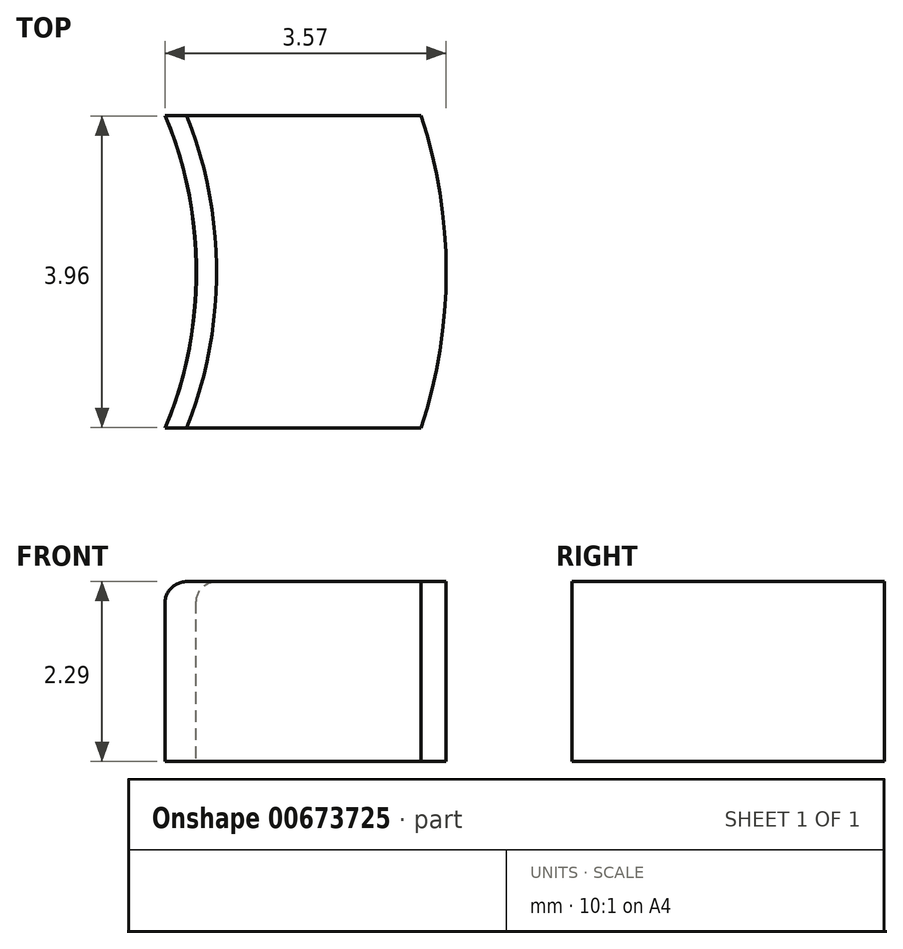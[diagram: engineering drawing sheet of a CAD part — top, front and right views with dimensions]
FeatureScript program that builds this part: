
annotation { "Feature Type Name" : "Feature", "Feature Type Description" : "" }
export const myFeature = defineFeature(function(context is Context, id is Id, definition is map)
    precondition{}
    {
        {
            var Q0;
            Q0=qCreatedBy(makeId("Top.planeOp"),FACE);
            var sketch = newSketch(context, id + "F0", { "sketchPlane" : qUnion([Q0])});
            skCircle(sketch, "E0", {"center": v(0, 0) * mm, "radius": 6.35 * mm});
            skEllipse(sketch, "E1", {"center": v(0, 0) * mm, "majorRadius": 4.11 * mm, "minorRadius": 3.18 * mm, "majorAxis": v(0, 1)});
            skSolve(sketch);
        }
        {
            var Q0;
            Q0=makeQuery(id+"F0.imprint","IMPRINT",FACE,{"disambiguationData":[TD([[makeQuery(id+"F0.imprint","IMPRINT",EDGE,{"derivedFrom":sQuery(id+"F0.wireOp",EDGE,"E0")}),1.0]])]});
            extrude(context, id + "F1", {"entities" : qUnion([Q0]), "depth" : 2.3 * mm, "offsetDistance" : 25.4 * mm});
        }
        {
            var Q0;
            Q0=makeQuery(id+"F1.opExtrude","CAP_EDGE",EDGE,{"disambiguationData":[OSD([sQuery(id+"F0.wireOp",EDGE,"E1")])],"isStart":false});
            fillet(context, id + "F2", {"entities" : qUnion([Q0]), "radius" : 0.25 * mm, "tangentPropagation" : true, "allowEdgeOverflow" : false});
        }
        {
            var Q0;
            Q0=makeQuery(id+"F1.opExtrude","CAP_FACE",FACE,{"disambiguationData":[OSD([sQuery(id+"F0.wireOp",EDGE,"E0"),sQuery(id+"F0.wireOp",EDGE,"E1")])],"isStart":false});
            var sketch = newSketch(context, id + "F3", { "sketchPlane" : qUnion([Q0])});
            skLineSegment(sketch, "E2.bottom", {"start": v(7, -1.98) * mm, "end": v(-1.33, -1.98) * mm});
            skLineSegment(sketch, "E2.top", {"start": v(7, 1.98) * mm, "end": v(-1.33, 1.98) * mm});
            skLineSegment(sketch, "E2.left", {"start": v(7, -1.98) * mm, "end": v(7, 1.98) * mm});
            skLineSegment(sketch, "E2.right", {"start": v(-1.33, -1.98) * mm, "end": v(-1.33, 1.98) * mm});
            skPoint(sketch, "E2.middle", {"position": v(2.84, 0) * mm});
            skSolve(sketch);
        }
        {
            var Q0;
            Q0 = qSketchRegion(id + "F3", true);
            extrude(context, id + "F4", {"entities" : qUnion([Q0]), "operationType" : NewBodyOperationType.INTERSECT, "oppositeDirection" : true, "depth" : 2.3 * mm, "offsetDistance" : 25.4 * mm});
        }
    });
